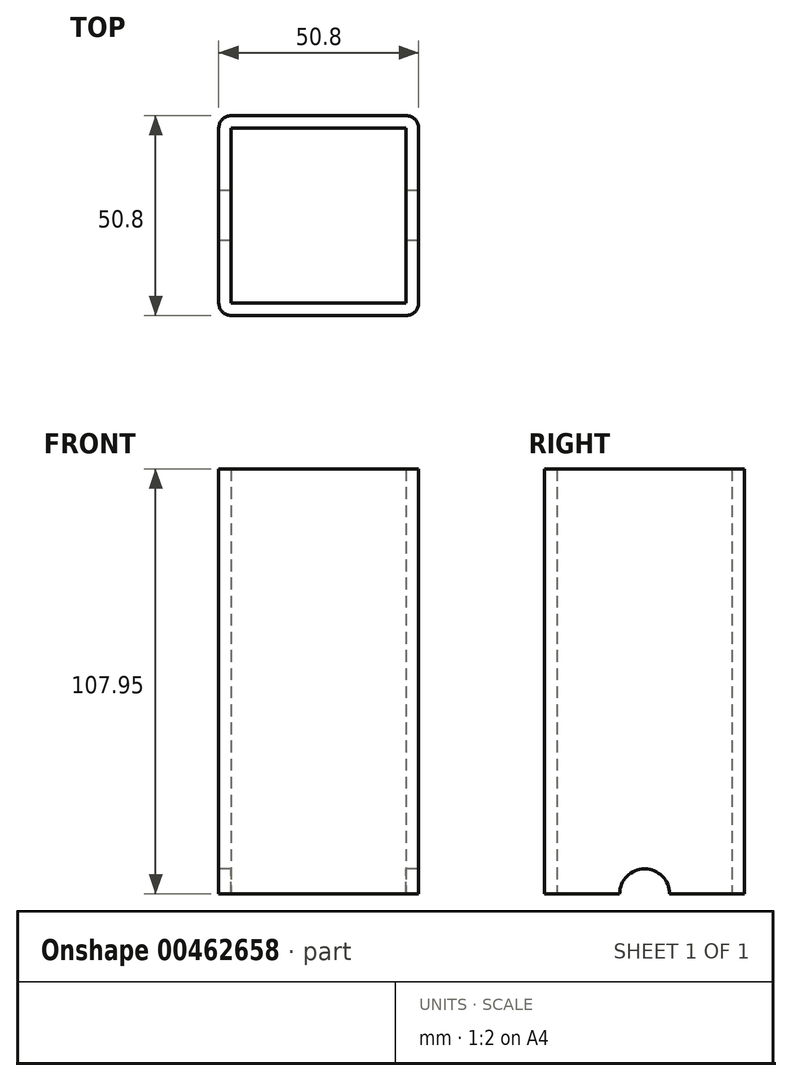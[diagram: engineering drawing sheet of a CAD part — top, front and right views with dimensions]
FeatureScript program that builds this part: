
annotation { "Feature Type Name" : "Feature", "Feature Type Description" : "" }
export const myFeature = defineFeature(function(context is Context, id is Id, definition is map)
    precondition{}
    {
        {
            var Q0;
            Q0=qCreatedBy(makeId("Top.planeOp"),FACE);
            var sketch = newSketch(context, id + "F0", { "sketchPlane" : qUnion([Q0])});
            skLineSegment(sketch, "E0.bottom", {"start": v(22.23, 25.4) * mm, "end": v(-22.23, 25.4) * mm});
            skLineSegment(sketch, "E0.top", {"start": v(22.23, -25.4) * mm, "end": v(-22.23, -25.4) * mm});
            skLineSegment(sketch, "E0.left", {"start": v(25.4, 22.23) * mm, "end": v(25.4, -22.23) * mm});
            skLineSegment(sketch, "E0.right", {"start": v(-25.4, 22.22) * mm, "end": v(-25.4, -22.23) * mm});
            skPoint(sketch, "E0.middle", {"position": v(0, 0) * mm});
            skPoint(sketch, "E1.visualSharp", {"position": v(-25.4, 25.4) * mm});
            skArc(sketch, "E1.filletArc", {"start": v(-22.23, 25.4) * mm, "mid": v(-24.47, 24.47) * mm, "end": v(-25.4, 22.23) * mm});
            skPoint(sketch, "E2.visualSharp", {"position": v(25.4, 25.4) * mm});
            skArc(sketch, "E2.filletArc", {"start": v(25.4, 22.23) * mm, "mid": v(24.47, 24.47) * mm, "end": v(22.23, 25.4) * mm});
            skPoint(sketch, "E3.visualSharp", {"position": v(25.4, -25.4) * mm});
            skArc(sketch, "E3.filletArc", {"start": v(22.23, -25.4) * mm, "mid": v(24.47, -24.47) * mm, "end": v(25.4, -22.23) * mm});
            skPoint(sketch, "E4.visualSharp", {"position": v(-25.4, -25.4) * mm});
            skArc(sketch, "E4.filletArc", {"start": v(-25.4, -22.23) * mm, "mid": v(-24.47, -24.47) * mm, "end": v(-22.23, -25.4) * mm});
            skLineSegment(sketch, "E5.0", {"start": v(22.23, 22.22) * mm, "end": v(22.23, 22.22) * mm});
            skLineSegment(sketch, "E5.1", {"start": v(22.23, 22.23) * mm, "end": v(22.23, -22.23) * mm});
            skLineSegment(sketch, "E5.2", {"start": v(22.23, 22.23) * mm, "end": v(-22.22, 22.23) * mm});
            skLineSegment(sketch, "E5.3", {"start": v(22.22, -22.22) * mm, "end": v(22.22, -22.22) * mm});
            skLineSegment(sketch, "E5.4", {"start": v(-22.23, 22.23) * mm, "end": v(-22.23, 22.23) * mm});
            skLineSegment(sketch, "E5.5", {"start": v(-22.22, 22.22) * mm, "end": v(-22.23, -22.23) * mm});
            skLineSegment(sketch, "E5.6", {"start": v(-22.22, -22.22) * mm, "end": v(-22.22, -22.22) * mm});
            skLineSegment(sketch, "E5.7", {"start": v(22.23, -22.23) * mm, "end": v(-22.23, -22.23) * mm});
            skSolve(sketch);
        }
        {
            var Q0;
            Q0=makeQuery(id+"F0.imprint","IMPRINT",FACE,{"disambiguationData":[TD([[makeQuery(id+"F0.imprint","IMPRINT",EDGE,{"derivedFrom":sQuery(id+"F0.wireOp",EDGE,"E0.bottom")}),1.0]])]});
            extrude(context, id + "F1", {"entities" : qUnion([Q0]), "depth" : 107.95 * mm});
        }
        {
            var Q0;
            Q0=makeQuery(id+"F1.opExtrude","SWEPT_FACE",FACE,{"disambiguationData":[OSD([sQuery(id+"F0.wireOp",EDGE,"E0.left")])]});
            var sketch = newSketch(context, id + "F2", { "sketchPlane" : qUnion([Q0])});
            skPoint(sketch, "E6", {"position": v(0, 0) * mm});
            skSolve(sketch);
        }
        {
            var Q0;
            Q0=sQuery(id+"F2.wireOp",VERTEX,"E6");
            var Q1;
            Q1=makeQuery(id+"F1.opExtrude","SWEPT_BODY",BODY,{"disambiguationData":[OSD([sQuery(id+"F0.wireOp",EDGE,"E0.bottom"),sQuery(id+"F0.wireOp",EDGE,"E0.top"),sQuery(id+"F0.wireOp",EDGE,"E0.left"),sQuery(id+"F0.wireOp",EDGE,"E0.right"),sQuery(id+"F0.wireOp",EDGE,"E1.filletArc"),sQuery(id+"F0.wireOp",EDGE,"E2.filletArc"),sQuery(id+"F0.wireOp",EDGE,"E3.filletArc"),sQuery(id+"F0.wireOp",EDGE,"E4.filletArc"),sQuery(id+"F0.wireOp",EDGE,"E5.1"),sQuery(id+"F0.wireOp",EDGE,"E5.2"),sQuery(id+"F0.wireOp",EDGE,"E5.5"),sQuery(id+"F0.wireOp",EDGE,"E5.7")])]});
            hole(context, id + "F3", {"style" : HoleStyle.SIMPLE, "endStyle" : HoleEndStyle.THROUGH, "holeDiameter" : 12.7 * mm, "isTappedThrough" : true, "tappedDepth" : 12.7 * mm, "tapClearance" : 3, "locations" : qUnion([Q0]), "scope" : qUnion([Q1])});
        }
    });
